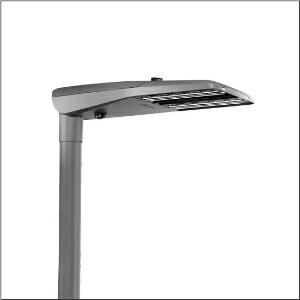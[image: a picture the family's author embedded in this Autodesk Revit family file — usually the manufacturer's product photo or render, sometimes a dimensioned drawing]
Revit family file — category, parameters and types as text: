
# Revit family: streetlight_sl_11_iq_midi___st1_2p1_0_5xc3g51y08me_d530
name_source: partatom
category: Lighting Fixtures
units: mm (PartAtom-declared; Revit-internal decimal feet)

## family parameters
Cut with Voids When Loaded = No
Host = Face
Light Source = No
Part Type = Normal
Room Calculation Point = No
Round Connector Dimension = Use Diameter
Shared = No

## types (1)
- --- (1 x LED, 17750 lm, 122.7 W, 3000K)
    Apparent Load = 123 VA
    CIE Flux Codes = 31 68 95 100 100
    Color Rendering = 70
    Color Temperature = 3000K
    Default Elevation = 1800 mm
    Description = Streetlight SL 11 iQ midi, mast luminaire, primary light control with 3 zone facetted reflector, of plastic, silver coated, highly specular, primary optical cover: cover, of PMMA, transparent, light distribution: ST1.2P1.0, light emission: direct distribution, primary light characteristic: asymmetric, installation type: post-top, side-entry, LED, High Power LED, rated luminous flux: 17.750lm, luminous efficacy: 145lm/W, light colour: 730, colour temperature: 3000K, control: presetting dimming logarithmic, Street-Remote, Auto-Match, Temp-Guard, Lumen-Switch, Night-Set, Smart-Wire, Light-Fading, Desk-Remote (wireless, voltage-free reading and setting of iQ features in the workshop via application-optimized NFC function/RFID function), optimised constant luminous flux control (CLO 2.0), with cable H07RN-F 5x 1.5mm², mains connection: 230..240V, AC, 50/60Hz, connection cable pre-assembled, cable length: 12,5m, start of lifetime: 123W, end of service life: 130W, reduction: 56W, luminaire housing, of diecast aluminium, powder-coated, Siteco® metallic grey (DB 702S), please order mast flange separately, inclination adjustable without tools: 0°, 5°, 10°, 15° (post-top) | 0°, -5°, -10°, -15° (side-entry), sealing non-destructively replaceable, multi-level sealing system, length: 780mm, width: 376mm, height: 118mm, mast flange for spigot size: 42mm (side-entry): 5XC10008XM4, 60/48mm (side-entry/post-top): 5XC10108XM2, 76/60mm (side-entry/post-top): 5XC10108XM1, equipment: Power, Smart Interface below and above, protection rating (complete): IP66, insulation class (complete): insulation class II (safety insulation), certification: CE, ENEC, VDE, UKCA, impact resistance: IK09, permissible operating ambient temperature for outdoor applications: -25..+50°C, standard-compliant lighting for roads and squares, Environmental Product Declaration (EPD) tested and certified by an independent institute, packaging unit: 1 piece

Light Distribution: ST1.2P1.0
    Height = 118 mm
    Lamp = 1 x LED
    Lamp Light Flux = 17750 lm
    Lamp Power = 122.7 W
    Lamp count = 1
    Length = 780 mm
    Luminous efficacy = 145 lm/W
    Manufacturer = Siteco
    ModVariant = No
    Model = 5XC3G51Y08ME
    Number of Poles = 1
    OnlyDefault = Yes
    Power Factor = 1
    Product Name = Streetlight SL 11 iQ midi | ST1.2P1.0
    Product group = mast luminaire | pylon top
    ProductGroupID = 6100
    Protection Class = Protection class II
    Protection Degree = IP 66
    RLX_Detail_Level = 1
    RLX_Emergency_Light_Flux = 0 lm
    RLX_Emergency_Type = 0
    RLX_Emergency_Type_DB = No
    RlxData = <blob elided: 69677 chars, md5=d682c7df>
    Socket = socket
    Standby Power = 0 W
    System Light Flux = 17750 lm
    System Power = 123 W
    Type Comments = factory setting: luminous flux: 100 % | dim-lin: 254 | 553 mA
    Type Image = l_1004429.jpg
    URL = http://relux.com
    VarID = @adj_064333
    Voltage = 0 V
    Weight = 0.00 kg
    Width = 376 mm

## geometry (parser evidence)
native form markers: Blend x4, Sweep x10
no freeform markers — native parametric forms only
